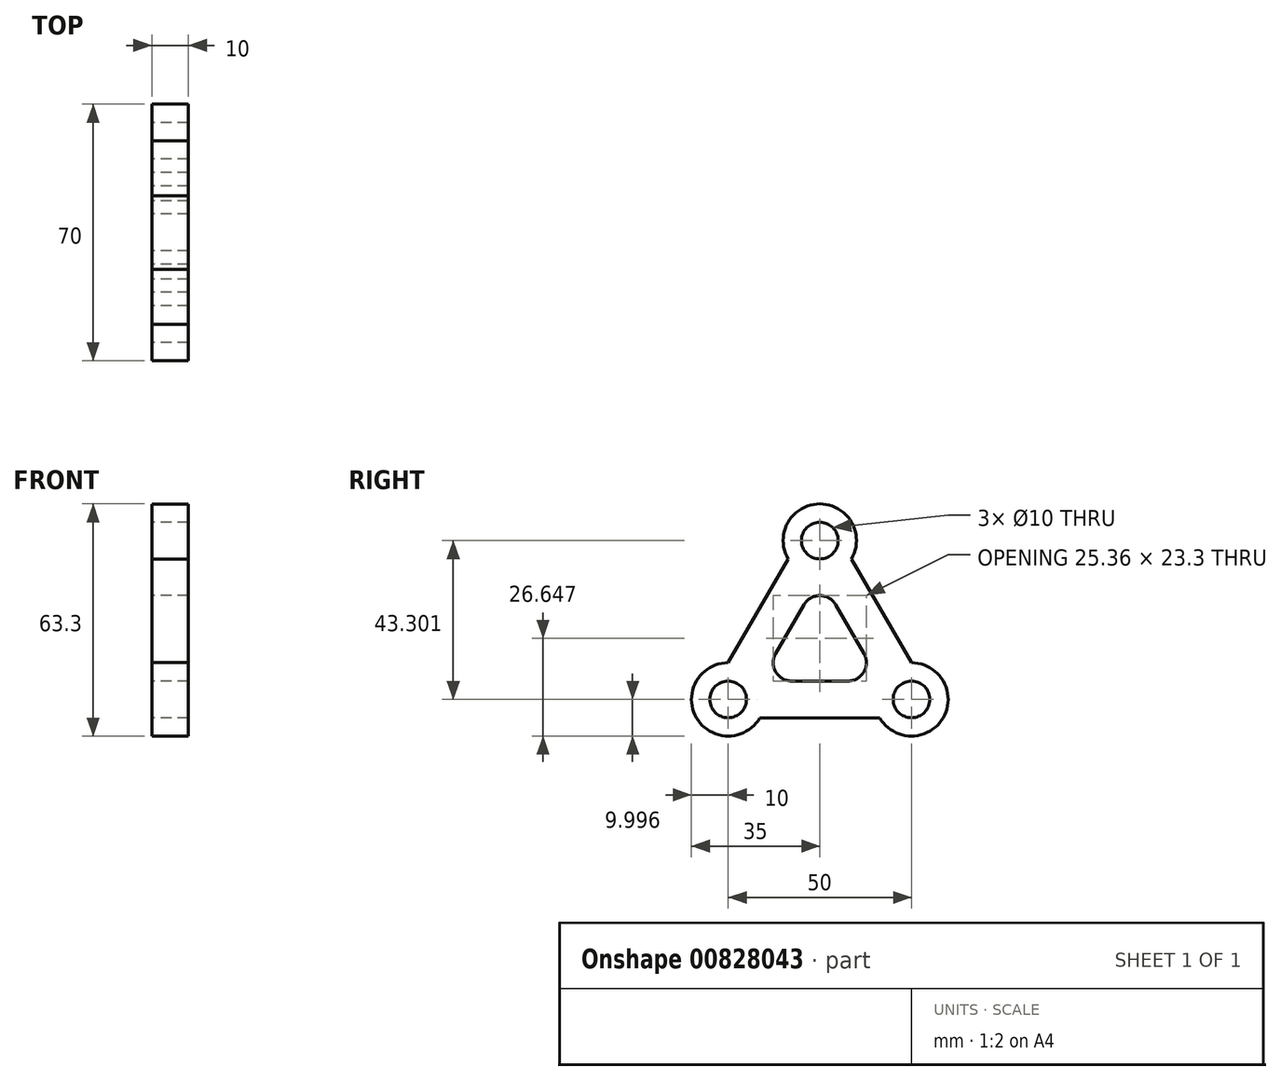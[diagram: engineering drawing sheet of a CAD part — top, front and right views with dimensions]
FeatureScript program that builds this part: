
annotation { "Feature Type Name" : "Feature", "Feature Type Description" : "" }
export const myFeature = defineFeature(function(context is Context, id is Id, definition is map)
    precondition{}
    {
        {
            var Q0;
            Q0=qCreatedBy(makeId("Right.planeOp"),FACE);
            var sketch = newSketch(context, id + "F0", { "sketchPlane" : qUnion([Q0])});
            skCircle(sketch, "E0.cCircle", {"center": v(0, 0) * mm, "radius": 14.43 * mm, "construction": true});
            skLineSegment(sketch, "E0.0", {"start": v(20, -14.43) * mm, "end": v(19.23, -14.43) * mm, "construction": true});
            skLineSegment(sketch, "E0.1", {"start": v(-22.5, -10.1) * mm, "end": v(-22.11, -9.43) * mm, "construction": true});
            skLineSegment(sketch, "E0.2", {"start": v(2.5, 24.54) * mm, "end": v(2.89, 23.87) * mm, "construction": true});
            skPoint(sketch, "E0.0.midPoint", {"position": v(0, -14.43) * mm});
            skCircle(sketch, "E1", {"center": v(0, 28.87) * mm, "radius": 5 * mm});
            skCircle(sketch, "E2.1.0", {"center": v(-25, -14.43) * mm, "radius": 5 * mm});
            skCircle(sketch, "E2.2.0", {"center": v(25, -14.43) * mm, "radius": 5 * mm});
            skArc(sketch, "E3", {"start": v(8.66, 23.87) * mm, "mid": v(0, 38.87) * mm, "end": v(-8.66, 23.87) * mm});
            skArc(sketch, "E4.1.0", {"start": v(-25, -4.43) * mm, "mid": v(-33.66, -19.43) * mm, "end": v(-16.34, -19.43) * mm});
            skArc(sketch, "E4.2.0", {"start": v(16.34, -19.43) * mm, "mid": v(33.66, -19.43) * mm, "end": v(25, -4.43) * mm});
            skLineSegment(sketch, "E5.0", {"start": v(-25, -4.43) * mm, "end": v(-8.66, 23.87) * mm});
            skLineSegment(sketch, "E6.0", {"start": v(8.66, 23.87) * mm, "end": v(25, -4.43) * mm});
            skLineSegment(sketch, "E7.0", {"start": v(16.34, -19.43) * mm, "end": v(-16.34, -19.43) * mm});
            skPoint(sketch, "E8.orphan", {"position": v(-4.33, 31.37) * mm});
            skLineSegment(sketch, "E9.trimOffspring", {"start": v(-2.89, 23.87) * mm, "end": v(-2.5, 24.54) * mm, "construction": true});
            skLineSegment(sketch, "E10.trimOffspring", {"start": v(4.33, 11.37) * mm, "end": v(12, -1.93) * mm});
            skLineSegment(sketch, "E11.trimOffspring", {"start": v(12.5, 7.22) * mm, "end": v(22.5, -10.1) * mm, "construction": true});
            skPoint(sketch, "E12.trimOffspring.end.orphan", {"position": v(4.33, 26.37) * mm});
            skLineSegment(sketch, "E13.trimOffspring", {"start": v(-20, -5.77) * mm, "end": v(-5, 20.2) * mm, "construction": true});
            skPoint(sketch, "E14.orphan", {"position": v(-29.33, -11.93) * mm});
            skLineSegment(sketch, "E15.trimOffspring", {"start": v(-12, -1.93) * mm, "end": v(-4.33, 11.37) * mm});
            skPoint(sketch, "E16.MirrorCS.start.orphan", {"position": v(-20.67, -16.93) * mm});
            skLineSegment(sketch, "E17.trimOffspring", {"start": v(7.68, -9.43) * mm, "end": v(-7.68, -9.43) * mm});
            skLineSegment(sketch, "E18.trimOffspring", {"start": v(15, -14.43) * mm, "end": v(-15, -14.43) * mm, "construction": true});
            skPoint(sketch, "E19.visualSharp", {"position": v(0, 18.87) * mm});
            skArc(sketch, "E19.filletArc", {"start": v(4.33, 11.37) * mm, "mid": v(0, 13.87) * mm, "end": v(-4.33, 11.37) * mm});
            skPoint(sketch, "E20.visualSharp", {"position": v(-16.34, -9.43) * mm});
            skArc(sketch, "E20.filletArc", {"start": v(-12, -1.93) * mm, "mid": v(-12, -6.93) * mm, "end": v(-7.68, -9.43) * mm});
            skPoint(sketch, "E21.visualSharp", {"position": v(16.34, -9.43) * mm});
            skArc(sketch, "E21.filletArc", {"start": v(7.68, -9.43) * mm, "mid": v(12, -6.93) * mm, "end": v(12, -1.93) * mm});
            skSolve(sketch);
        }
        {
            var Q0;
            Q0=makeQuery(id+"F0.imprint","IMPRINT",FACE,{"disambiguationData":[TD([[makeQuery(id+"F0.imprint","IMPRINT",EDGE,{"derivedFrom":sQuery(id+"F0.wireOp",EDGE,"E1")}),-1.0]])]});
            extrude(context, id + "F1", {"entities" : qUnion([Q0]), "depth" : 10 * mm, "offsetDistance" : 25 * mm});
        }
    });
